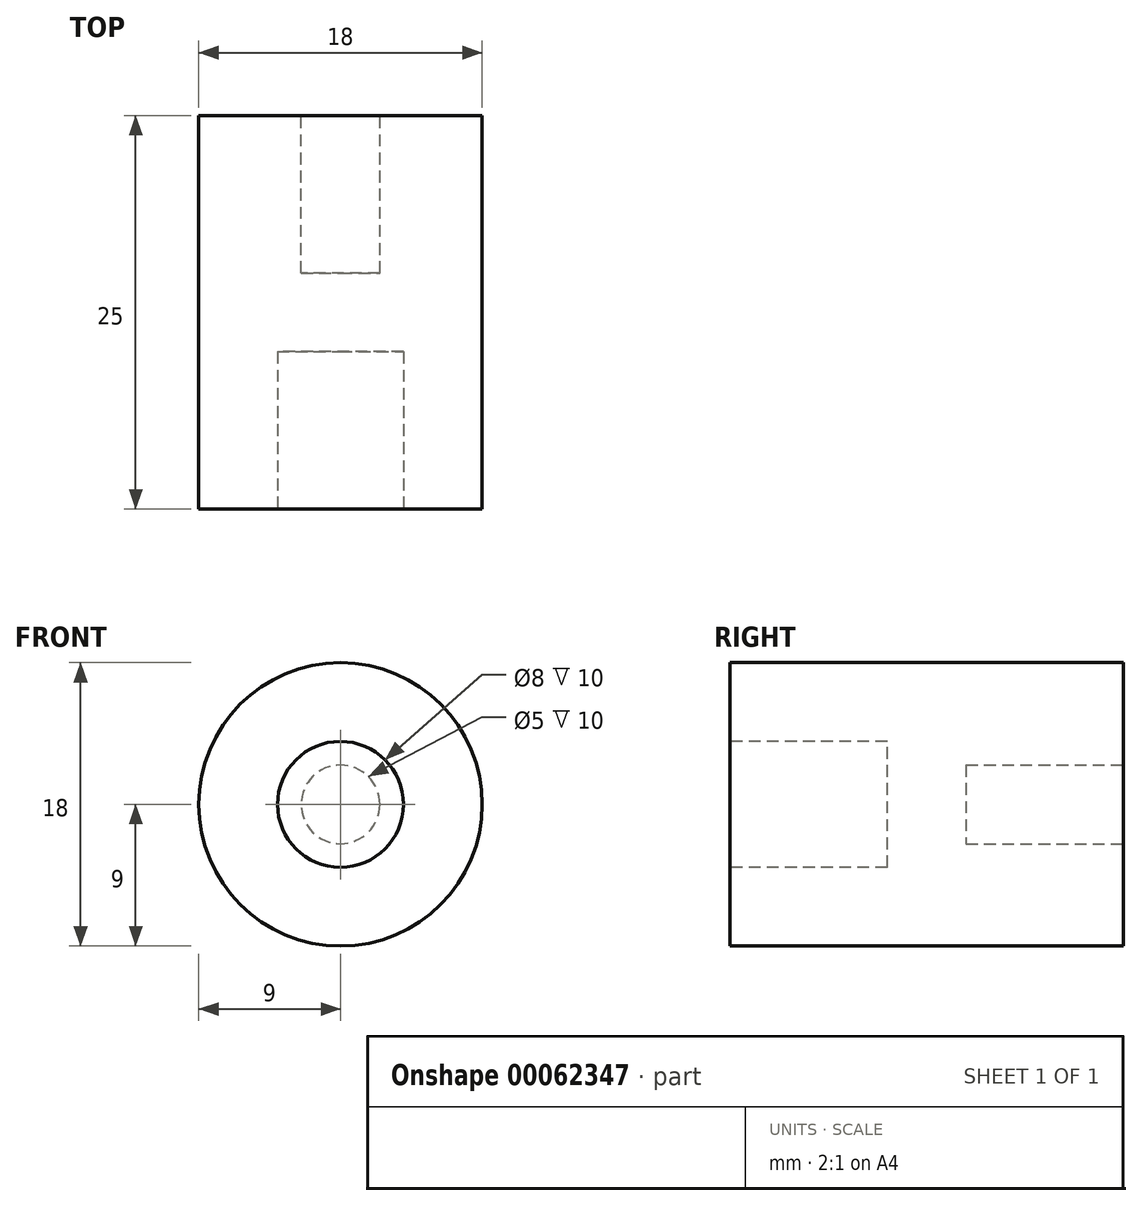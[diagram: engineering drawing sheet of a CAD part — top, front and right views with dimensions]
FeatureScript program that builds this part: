
annotation { "Feature Type Name" : "Feature", "Feature Type Description" : "" }
export const myFeature = defineFeature(function(context is Context, id is Id, definition is map)
    precondition{}
    {
        {
            var Q0;
            Q0=qCreatedBy(makeId("Front.planeOp"),FACE);
            var sketch = newSketch(context, id + "F0", { "sketchPlane" : qUnion([Q0])});
            skCircle(sketch, "E0", {"center": v(0, 0) * mm, "radius": 9 * mm});
            skSolve(sketch);
        }
        {
            var Q0;
            Q0=makeQuery(id+"F0.imprint","IMPRINT",FACE,{"disambiguationData":[TD([[makeQuery(id+"F0.imprint","IMPRINT",EDGE,{"derivedFrom":sQuery(id+"F0.wireOp",EDGE,"E0")}),1.0]])]});
            extrude(context, id + "F1", {"entities" : qUnion([Q0]), "endBound" : BoundingType.SYMMETRIC, "depth" : 25 * mm});
        }
        {
            var Q0;
            Q0=makeQuery(id+"F1.opExtrude","CAP_FACE",FACE,{"disambiguationData":[OSD([sQuery(id+"F0.wireOp",EDGE,"E0")])],"isStart":false});
            var sketch = newSketch(context, id + "F2", { "sketchPlane" : qUnion([Q0])});
            skCircle(sketch, "E1", {"center": v(0, 0) * mm, "radius": 4 * mm});
            skSolve(sketch);
        }
        {
            var Q0;
            Q0 = qSketchRegion(id + "F2", true);
            extrude(context, id + "F3", {"entities" : qUnion([Q0]), "operationType" : NewBodyOperationType.REMOVE, "oppositeDirection" : true, "depth" : 10 * mm});
        }
        {
            var Q0;
            Q0=makeQuery(id+"F1.opExtrude","CAP_FACE",FACE,{"disambiguationData":[OSD([sQuery(id+"F0.wireOp",EDGE,"E0")])],"isStart":true});
            var sketch = newSketch(context, id + "F4", { "sketchPlane" : qUnion([Q0])});
            skCircle(sketch, "E2", {"center": v(0, 0) * mm, "radius": 2.5 * mm});
            skSolve(sketch);
        }
        {
            var Q0;
            Q0 = qSketchRegion(id + "F4", true);
            extrude(context, id + "F5", {"entities" : qUnion([Q0]), "operationType" : NewBodyOperationType.REMOVE, "oppositeDirection" : true, "depth" : 10 * mm});
        }
    });
